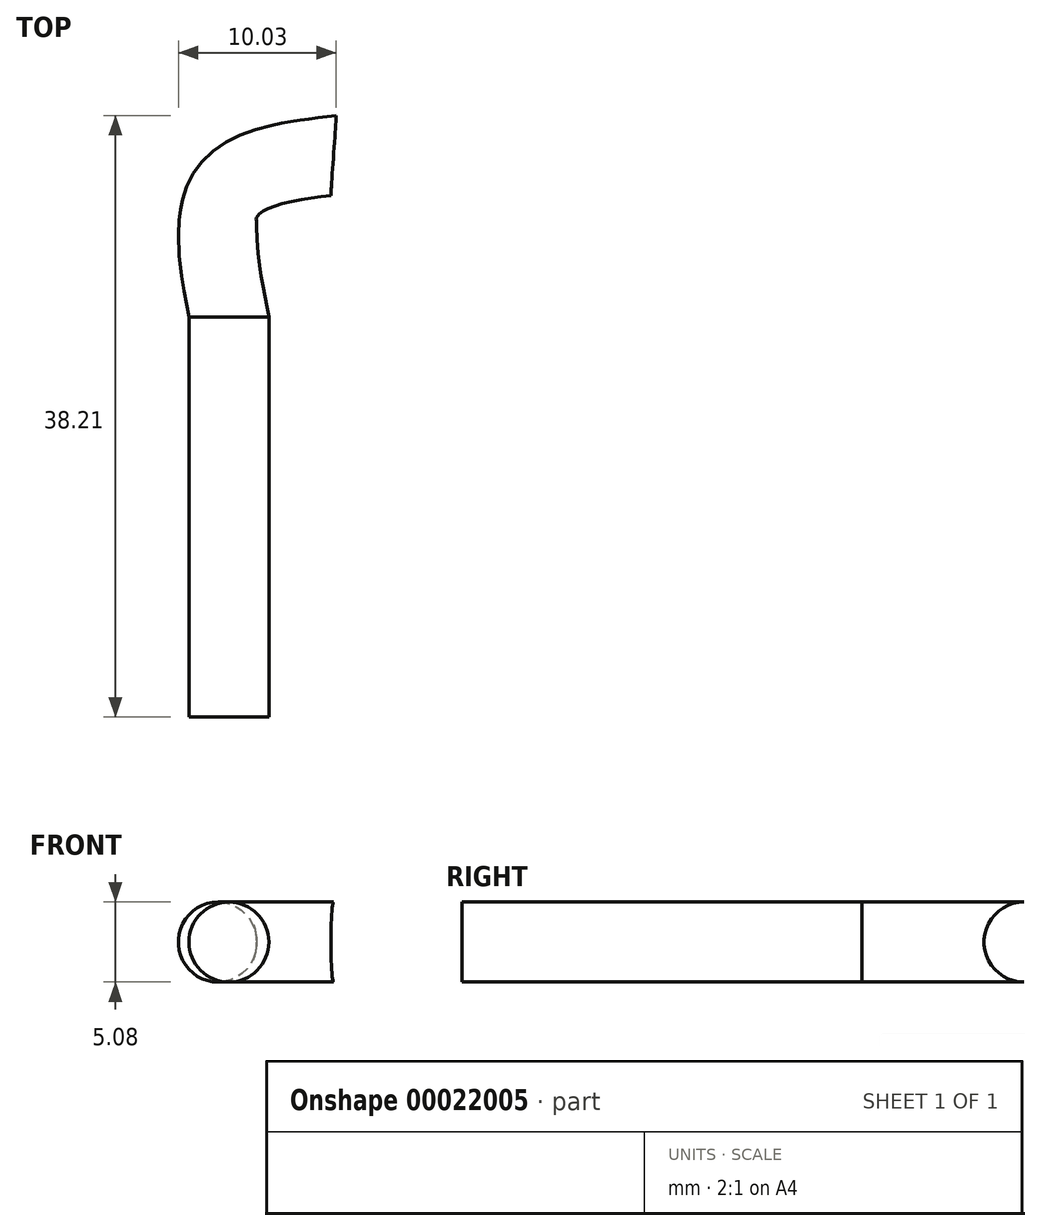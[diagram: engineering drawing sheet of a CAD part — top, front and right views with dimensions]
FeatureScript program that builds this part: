
annotation { "Feature Type Name" : "Feature", "Feature Type Description" : "" }
export const myFeature = defineFeature(function(context is Context, id is Id, definition is map)
    precondition{}
    {
        {
            var Q0;
            Q0=qCreatedBy(makeId("Front.planeOp"),FACE);
            var sketch = newSketch(context, id + "F0", { "sketchPlane" : qUnion([Q0])});
            skCircle(sketch, "E0", {"center": v(0, 0) * mm, "radius": 2.54 * mm});
            skSolve(sketch);
        }
        {
            var Q0;
            Q0 = qSketchRegion(id + "F0", true);
            extrude(context, id + "F1", {"entities" : qUnion([Q0]), "depth" : 25.4 * mm});
        }
        {
            var Q0;
            Q0=qCreatedBy(makeId("Top.planeOp"),FACE);
            var sketch = newSketch(context, id + "F2", { "sketchPlane" : qUnion([Q0])});
            skFitSpline(sketch, "E1", {"points": [v(0, 0) * mm, v(0, 8) * mm, v(6.65, 10.27) * mm], "startDerivative": vector(-3.54, 18.26) * mm, "endDerivative": vector(17.06, 2.1) * mm});
            skSolve(sketch);
        }
        {
            var Q0;
            Q0=makeQuery(id+"F1.opExtrude","CAP_FACE",FACE,{"disambiguationData":[OSD([sQuery(id+"F0.wireOp",EDGE,"E0")])],"isStart":true});
            var Q1;
            Q1=sQuery(id+"F2.wireOp",EDGE,"E1");
            sweep(context, id + "F3", {"operationType" : NewBodyOperationType.ADD, "profiles" : qUnion([Q0]), "path" : qUnion([Q1])});
        }
    });
